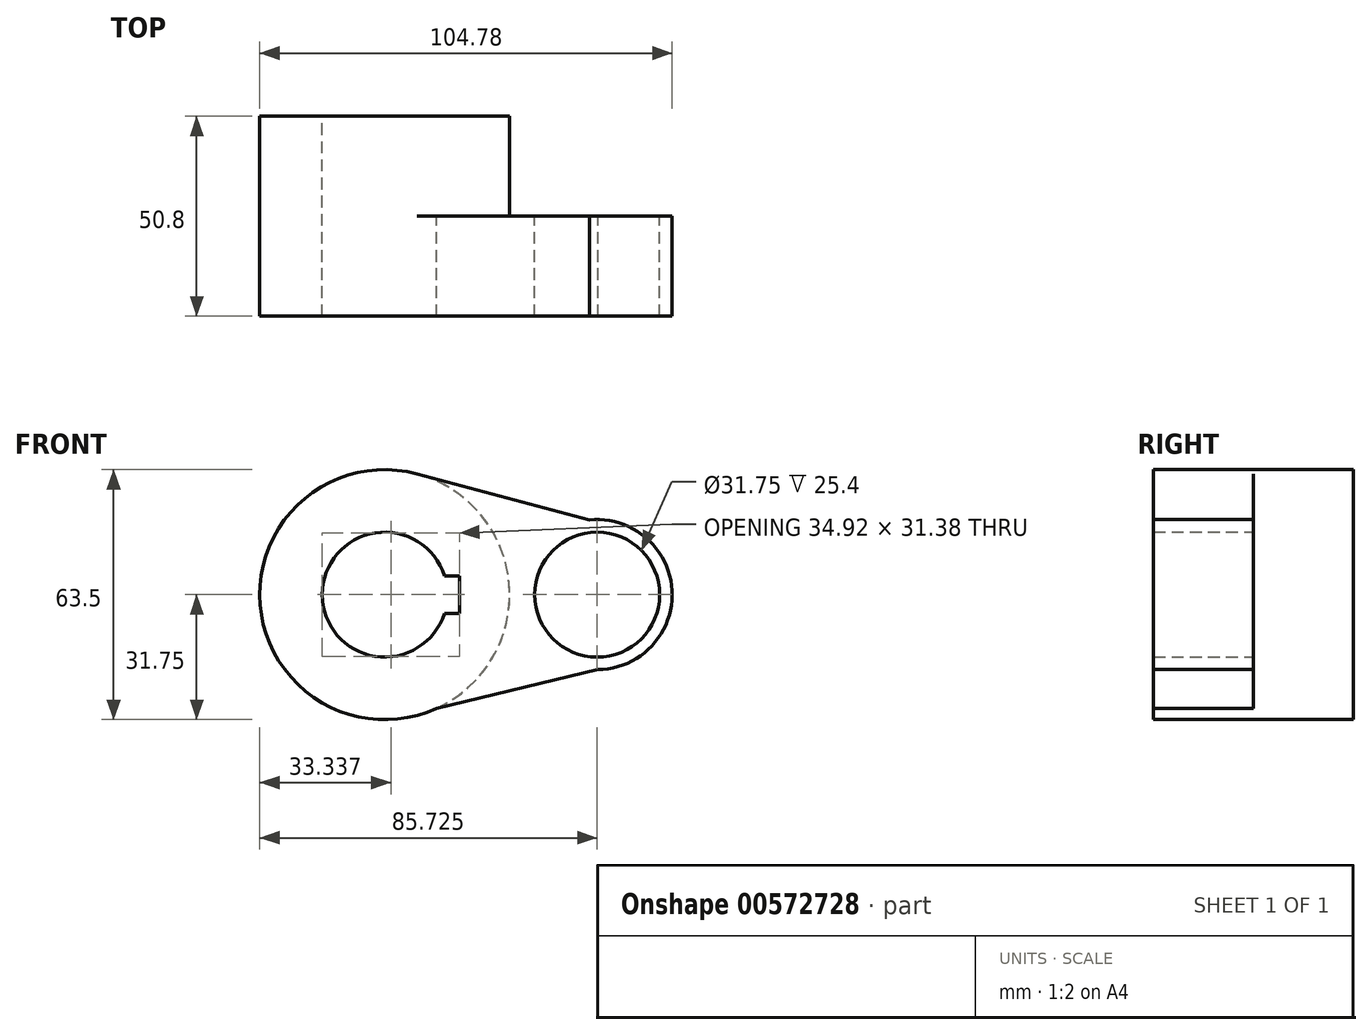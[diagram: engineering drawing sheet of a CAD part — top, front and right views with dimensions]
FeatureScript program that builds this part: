
annotation { "Feature Type Name" : "Feature", "Feature Type Description" : "" }
export const myFeature = defineFeature(function(context is Context, id is Id, definition is map)
    precondition{}
    {
        {
            var Q0;
            Q0=qCreatedBy(makeId("Front.planeOp"),FACE);
            var sketch = newSketch(context, id + "F0", { "sketchPlane" : qUnion([Q0])});
            skCircle(sketch, "E0", {"center": v(0, 0) * mm, "radius": 31.75 * mm});
            skCircle(sketch, "E1", {"center": v(53.97, 0) * mm, "radius": 19.05 * mm});
            skCircle(sketch, "E2", {"center": v(0, 0) * mm, "radius": 15.88 * mm});
            skCircle(sketch, "E3", {"center": v(53.97, 0) * mm, "radius": 15.88 * mm});
            skLineSegment(sketch, "E4.bottom", {"start": v(19.05, -4.76) * mm, "end": v(-19.05, -4.76) * mm});
            skLineSegment(sketch, "E4.top", {"start": v(19.05, 4.76) * mm, "end": v(-19.05, 4.76) * mm});
            skLineSegment(sketch, "E4.left", {"start": v(19.05, -4.76) * mm, "end": v(19.05, 4.76) * mm});
            skLineSegment(sketch, "E4.right", {"start": v(-19.05, -4.76) * mm, "end": v(-19.05, 4.76) * mm});
            skLineSegment(sketch, "E5", {"start": v(8.21, 30.67) * mm, "end": v(51.98, 18.95) * mm});
            skLineSegment(sketch, "E6", {"start": v(13.16, -28.9) * mm, "end": v(54.16, -19.05) * mm});
            skSolve(sketch);
        }
        {
            var Q0;
            {var subQ4=sQuery(id+"F0.wireOp",EDGE,"E4.left");Q0=makeQuery(id+"F0.imprint","IMPRINT",FACE,{"disambiguationData":[TD([[makeQuery(id+"F0.imprint","IMPRINT",EDGE,{"derivedFrom":subQ4}),-1.0]])]});}
            var Q1;
            Q1=makeQuery(id+"F0.imprint","IMPRINT",FACE,{"disambiguationData":[TD([[makeQuery(id+"F0.imprint","IMPRINT",EDGE,{"derivedFrom":sQuery(id+"F0.wireOp",EDGE,"E3")}),-1.0]])]});
            var Q2;
            {var subQ0=sQuery(id+"F0.wireOp",EDGE,"E5");Q2=makeQuery(id+"F0.imprint","IMPRINT",FACE,{"disambiguationData":[TD([[makeQuery(id+"F0.imprint","IMPRINT",EDGE,{"derivedFrom":subQ0}),-1.0]])]});}
            var Q3;
            {var subQ5=sQuery(id+"F0.wireOp",EDGE,"E4.right");Q3=makeQuery(id+"F0.imprint","IMPRINT",FACE,{"disambiguationData":[TD([[makeQuery(id+"F0.imprint","IMPRINT",EDGE,{"derivedFrom":subQ5}),-1.0]])]});}
            extrude(context, id + "F1", {"entities" : qUnion([Q0, Q1, Q2, Q3]), "depth" : 25.4 * mm, "offsetDistance" : 25.4 * mm});
        }
        {
            var Q0;
            {var subQ4=sQuery(id+"F0.wireOp",EDGE,"E4.left");Q0=makeQuery(id+"F0.imprint","IMPRINT",FACE,{"disambiguationData":[TD([[makeQuery(id+"F0.imprint","IMPRINT",EDGE,{"derivedFrom":subQ4}),-1.0]])]});}
            var Q1;
            {var subQ5=sQuery(id+"F0.wireOp",EDGE,"E4.right");Q1=makeQuery(id+"F0.imprint","IMPRINT",FACE,{"disambiguationData":[TD([[makeQuery(id+"F0.imprint","IMPRINT",EDGE,{"derivedFrom":subQ5}),-1.0]])]});}
            extrude(context, id + "F2", {"entities" : qUnion([Q0, Q1]), "operationType" : NewBodyOperationType.ADD, "oppositeDirection" : true, "depth" : 25.4 * mm, "offsetDistance" : 25.4 * mm});
        }
    });
